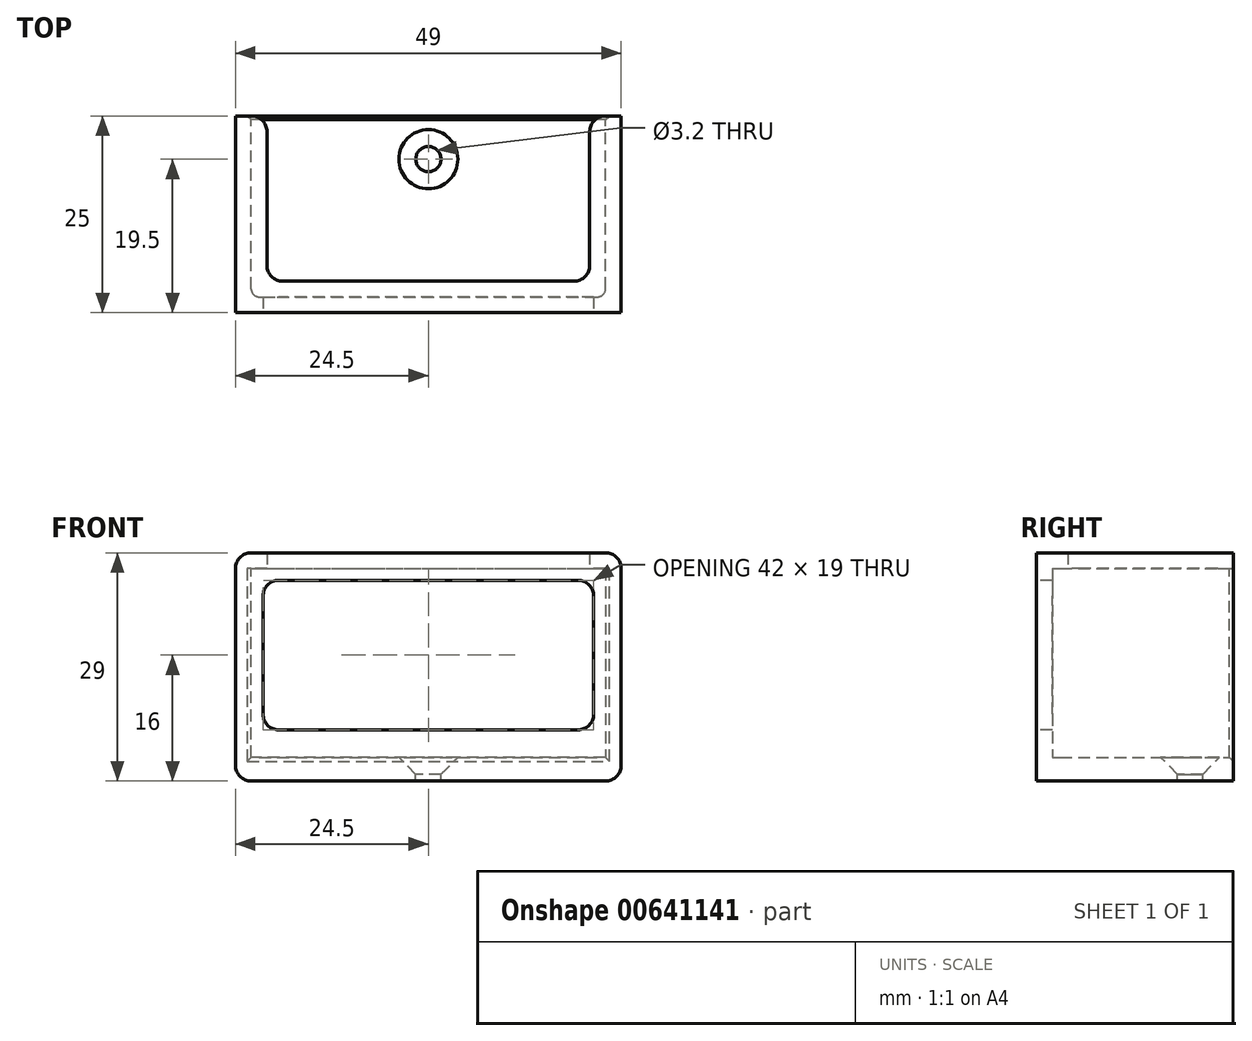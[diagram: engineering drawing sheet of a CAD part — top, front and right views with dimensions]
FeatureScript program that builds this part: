
annotation { "Feature Type Name" : "Feature", "Feature Type Description" : "" }
export const myFeature = defineFeature(function(context is Context, id is Id, definition is map)
    precondition{}
    {
        {
            var Q0;
            Q0=qCreatedBy(makeId("Top.planeOp"),FACE);
            var sketch = newSketch(context, id + "F0", { "sketchPlane" : qUnion([Q0])});
            skLineSegment(sketch, "E0.bottom", {"start": v(-22.5, -11.5) * mm, "end": v(22.5, -11.5) * mm});
            skLineSegment(sketch, "E0.left", {"start": v(-22.5, -11.5) * mm, "end": v(-22.5, 11.5) * mm});
            skLineSegment(sketch, "E0.right", {"start": v(22.5, -11.5) * mm, "end": v(22.5, 11.5) * mm});
            skPoint(sketch, "E0.middle", {"position": v(0, 0) * mm});
            skLineSegment(sketch, "E1.bottom", {"start": v(-24.5, -13.5) * mm, "end": v(24.5, -13.5) * mm});
            skLineSegment(sketch, "E1.left", {"start": v(-24.5, -13.5) * mm, "end": v(-24.5, 11.5) * mm});
            skLineSegment(sketch, "E1.right", {"start": v(24.5, -13.5) * mm, "end": v(24.5, 11.5) * mm});
            skLineSegment(sketch, "E2", {"start": v(-22.5, 11.5) * mm, "end": v(-24.5, 11.5) * mm});
            skLineSegment(sketch, "E3", {"start": v(22.5, 11.5) * mm, "end": v(24.5, 11.5) * mm});
            skPoint(sketch, "E4.orphan", {"position": v(-24.5, 13.5) * mm});
            skPoint(sketch, "E5.orphan", {"position": v(24.5, 13.5) * mm});
            skSolve(sketch);
        }
        {
            var Q0;
            Q0 = qSketchRegion(id + "F0", true);
            extrude(context, id + "F1", {"entities" : qUnion([Q0]), "depth" : 24 * mm, "offsetDistance" : 25 * mm});
        }
        {
            var Q0;
            Q0=makeQuery(id+"F1.opExtrude","CAP_FACE",FACE,{"disambiguationData":[OSD([sQuery(id+"F0.wireOp",EDGE,"E0.bottom"),sQuery(id+"F0.wireOp",EDGE,"E0.left"),sQuery(id+"F0.wireOp",EDGE,"E0.right"),sQuery(id+"F0.wireOp",EDGE,"E1.bottom"),sQuery(id+"F0.wireOp",EDGE,"E1.left"),sQuery(id+"F0.wireOp",EDGE,"E1.right"),sQuery(id+"F0.wireOp",EDGE,"E2"),sQuery(id+"F0.wireOp",EDGE,"E3")])],"isStart":false});
            var sketch = newSketch(context, id + "F2", { "sketchPlane" : qUnion([Q0])});
            skLineSegment(sketch, "E6.bottom", {"start": v(-24.5, -13.5) * mm, "end": v(24.5, -13.5) * mm});
            skLineSegment(sketch, "E6.top", {"start": v(-24.5, -9.5) * mm, "end": v(24.5, -9.5) * mm});
            skLineSegment(sketch, "E6.left", {"start": v(-24.5, -13.5) * mm, "end": v(-24.5, -9.5) * mm});
            skLineSegment(sketch, "E6.right", {"start": v(24.5, -13.5) * mm, "end": v(24.5, -9.5) * mm});
            skLineSegment(sketch, "E7.bottom", {"start": v(-24.5, 11.5) * mm, "end": v(-20.5, 11.5) * mm});
            skLineSegment(sketch, "E7.top", {"start": v(-24.5, -9.5) * mm, "end": v(-20.5, -9.5) * mm});
            skLineSegment(sketch, "E7.left", {"start": v(-24.5, 11.5) * mm, "end": v(-24.5, -9.5) * mm});
            skLineSegment(sketch, "E7.right", {"start": v(-20.5, 11.5) * mm, "end": v(-20.5, -9.5) * mm});
            skLineSegment(sketch, "E8.bottom", {"start": v(24.5, 11.5) * mm, "end": v(20.5, 11.5) * mm});
            skLineSegment(sketch, "E8.top", {"start": v(24.5, -9.5) * mm, "end": v(20.5, -9.5) * mm});
            skLineSegment(sketch, "E8.left", {"start": v(24.5, 11.5) * mm, "end": v(24.5, -9.5) * mm});
            skLineSegment(sketch, "E8.right", {"start": v(20.5, 11.5) * mm, "end": v(20.5, -9.5) * mm});
            skSolve(sketch);
        }
        {
            var Q0;
            Q0 = qSketchRegion(id + "F2", true);
            extrude(context, id + "F3", {"entities" : qUnion([Q0]), "operationType" : NewBodyOperationType.ADD, "depth" : 2 * mm, "offsetDistance" : 25 * mm});
        }
        {
            var Q0;
            Q0=makeQuery(id+"F3.boolean.opBoolean","MERGE",FACE,{"derivedFrom":[makeQuery(id+"F1.opExtrude","SWEPT_FACE",FACE,{"disambiguationData":[OSD([sQuery(id+"F0.wireOp",EDGE,"E1.bottom")])]}),makeQuery(id+"F3.opExtrude","SWEPT_FACE",FACE,{"disambiguationData":[OSD([sQuery(id+"F2.wireOp",EDGE,"E6.bottom")])]})]});
            var sketch = newSketch(context, id + "F4", { "sketchPlane" : qUnion([Q0])});
            skLineSegment(sketch, "E9.bottom", {"start": v(-21, 22.5) * mm, "end": v(21, 22.5) * mm});
            skLineSegment(sketch, "E9.top", {"start": v(-21, 3.5) * mm, "end": v(21, 3.5) * mm});
            skLineSegment(sketch, "E9.left", {"start": v(-21, 22.5) * mm, "end": v(-21, 3.5) * mm});
            skLineSegment(sketch, "E9.right", {"start": v(21, 22.5) * mm, "end": v(21, 3.5) * mm});
            skSolve(sketch);
        }
        {
            var Q0;
            Q0 = qSketchRegion(id + "F4", true);
            extrude(context, id + "F5", {"entities" : qUnion([Q0]), "operationType" : NewBodyOperationType.REMOVE, "oppositeDirection" : true, "depth" : 25 * mm, "offsetDistance" : 25 * mm});
        }
        {
            var Q0;
            Q0=makeQuery(id+"F1.opExtrude","CAP_FACE",FACE,{"disambiguationData":[OSD([sQuery(id+"F0.wireOp",EDGE,"E0.bottom"),sQuery(id+"F0.wireOp",EDGE,"E0.left"),sQuery(id+"F0.wireOp",EDGE,"E0.right"),sQuery(id+"F0.wireOp",EDGE,"E1.bottom"),sQuery(id+"F0.wireOp",EDGE,"E1.left"),sQuery(id+"F0.wireOp",EDGE,"E1.right"),sQuery(id+"F0.wireOp",EDGE,"E2"),sQuery(id+"F0.wireOp",EDGE,"E3")])],"isStart":true});
            var sketch = newSketch(context, id + "F6", { "sketchPlane" : qUnion([Q0])});
            skLineSegment(sketch, "E10.bottom", {"start": v(24.5, 13.5) * mm, "end": v(-24.5, 13.5) * mm});
            skLineSegment(sketch, "E10.top", {"start": v(24.5, -11.5) * mm, "end": v(-24.5, -11.5) * mm});
            skLineSegment(sketch, "E10.left", {"start": v(24.5, 13.5) * mm, "end": v(24.5, -11.5) * mm});
            skLineSegment(sketch, "E10.right", {"start": v(-24.5, 13.5) * mm, "end": v(-24.5, -11.5) * mm});
            skSolve(sketch);
        }
        {
            var Q0;
            Q0 = qSketchRegion(id + "F6", true);
            extrude(context, id + "F7", {"entities" : qUnion([Q0]), "operationType" : NewBodyOperationType.ADD, "depth" : 3 * mm, "offsetDistance" : 25 * mm});
        }
        {
            var Q0;
            Q0=makeQuery(id+"F5.boolean.opBoolean","COPY",EDGE,{"derivedFrom":makeQuery(id+"F5.opExtrude","SWEPT_EDGE",EDGE,{"disambiguationData":[OSD([sQuery(id+"F4.wireOp",EDGE,"E9.top"),sQuery(id+"F4.wireOp",EDGE,"E9.left")])]})});
            var Q1;
            Q1=makeQuery(id+"F5.boolean.opBoolean","COPY",EDGE,{"derivedFrom":makeQuery(id+"F5.opExtrude","SWEPT_EDGE",EDGE,{"disambiguationData":[OSD([sQuery(id+"F4.wireOp",EDGE,"E9.top"),sQuery(id+"F4.wireOp",EDGE,"E9.right")])]})});
            var Q2;
            Q2=makeQuery(id+"F5.boolean.opBoolean","COPY",EDGE,{"derivedFrom":makeQuery(id+"F5.opExtrude","SWEPT_EDGE",EDGE,{"disambiguationData":[OSD([sQuery(id+"F4.wireOp",EDGE,"E9.bottom"),sQuery(id+"F4.wireOp",EDGE,"E9.left")])]})});
            var Q3;
            Q3=makeQuery(id+"F5.boolean.opBoolean","COPY",EDGE,{"derivedFrom":makeQuery(id+"F5.opExtrude","SWEPT_EDGE",EDGE,{"disambiguationData":[OSD([sQuery(id+"F4.wireOp",EDGE,"E9.bottom"),sQuery(id+"F4.wireOp",EDGE,"E9.right")])]})});
            var Q4;
            Q4=makeQuery(id+"F7.opExtrude","CAP_EDGE",EDGE,{"disambiguationData":[OSD([sQuery(id+"F6.wireOp",EDGE,"E10.right")])],"isStart":false});
            var Q5;
            Q5=makeQuery(id+"F7.opExtrude","CAP_EDGE",EDGE,{"disambiguationData":[OSD([sQuery(id+"F6.wireOp",EDGE,"E10.left")])],"isStart":false});
            var Q6;
            Q6=makeQuery(id+"F3.opExtrude","SWEPT_EDGE",EDGE,{"disambiguationData":[OSD([sQuery(id+"F2.wireOp",EDGE,"E6.top"),sQuery(id+"F2.wireOp",EDGE,"E7.top"),sQuery(id+"F2.wireOp",EDGE,"E7.right")])]});
            var Q7;
            Q7=makeQuery(id+"F3.opExtrude","SWEPT_EDGE",EDGE,{"disambiguationData":[OSD([sQuery(id+"F2.wireOp",EDGE,"E6.top"),sQuery(id+"F2.wireOp",EDGE,"E8.top"),sQuery(id+"F2.wireOp",EDGE,"E8.right")])]});
            var Q8;
            Q8=makeQuery(id+"F3.opExtrude","SWEPT_EDGE",EDGE,{"disambiguationData":[OSD([sQuery(id+"F2.wireOp",EDGE,"E8.bottom"),sQuery(id+"F2.wireOp",EDGE,"E8.right")])]});
            var Q9;
            Q9=makeQuery(id+"F3.opExtrude","SWEPT_EDGE",EDGE,{"disambiguationData":[OSD([sQuery(id+"F2.wireOp",EDGE,"E7.bottom"),sQuery(id+"F2.wireOp",EDGE,"E7.right")])]});
            var Q10;
            Q10=makeQuery(id+"F3.opExtrude","CAP_EDGE",EDGE,{"disambiguationData":[OSD([sQuery(id+"F2.wireOp",EDGE,"E6.right"),sQuery(id+"F2.wireOp",EDGE,"E8.left")])],"isStart":false});
            var Q11;
            Q11=makeQuery(id+"F3.opExtrude","CAP_EDGE",EDGE,{"disambiguationData":[OSD([sQuery(id+"F2.wireOp",EDGE,"E6.left"),sQuery(id+"F2.wireOp",EDGE,"E7.left")])],"isStart":false});
            fillet(context, id + "F8", {"entities" : qUnion([Q0, Q1, Q2, Q3, Q4, Q5, Q6, Q7, Q8, Q9, Q10, Q11]), "radius" : 2 * mm, "tangentPropagation" : true, "allowEdgeOverflow" : false});
        }
        {
            var Q0;
            Q0=makeQuery(id+"F7.opExtrude","CAP_FACE",FACE,{"disambiguationData":[OSD([sQuery(id+"F6.wireOp",EDGE,"E10.bottom"),sQuery(id+"F6.wireOp",EDGE,"E10.top"),sQuery(id+"F6.wireOp",EDGE,"E10.left"),sQuery(id+"F6.wireOp",EDGE,"E10.right")])],"isStart":true});
            var sketch = newSketch(context, id + "F9", { "sketchPlane" : qUnion([Q0])});
            skLineSegment(sketch, "E11", {"start": v(0, 0) * mm, "end": v(0, 6) * mm});
            skSolve(sketch);
        }
        {
            var Q0;
            Q0=sQuery(id+"F9.wireOp",VERTEX,"E11.end");
            var Q1;
            Q1=makeQuery(id+"F1.opExtrude","SWEPT_BODY",BODY,{"disambiguationData":[OSD([sQuery(id+"F0.wireOp",EDGE,"E0.bottom"),sQuery(id+"F0.wireOp",EDGE,"E0.left"),sQuery(id+"F0.wireOp",EDGE,"E0.right"),sQuery(id+"F0.wireOp",EDGE,"E1.bottom"),sQuery(id+"F0.wireOp",EDGE,"E1.left"),sQuery(id+"F0.wireOp",EDGE,"E1.right"),sQuery(id+"F0.wireOp",EDGE,"E2"),sQuery(id+"F0.wireOp",EDGE,"E3")])]});
            hole(context, id + "F10", {"style" : HoleStyle.C_SINK, "endStyle" : HoleEndStyle.THROUGH, "holeDiameter" : 3.2 * mm, "cSinkDiameter" : 7.5 * mm, "cSinkAngle" : 90 * degree, "majorDiameter" : 5 * mm, "isTappedThrough" : true, "tappedDepth" : 12 * mm, "tapClearance" : 3, "locations" : qUnion([Q0]), "scope" : qUnion([Q1])});
        }
        {
            var Q0;
            Q0=makeQuery(id+"F1.opExtrude","SWEPT_EDGE",EDGE,{"disambiguationData":[OSD([sQuery(id+"F0.wireOp",EDGE,"E0.bottom"),sQuery(id+"F0.wireOp",EDGE,"E0.left")])]});
            var Q1;
            Q1=makeQuery(id+"F1.opExtrude","SWEPT_EDGE",EDGE,{"disambiguationData":[OSD([sQuery(id+"F0.wireOp",EDGE,"E0.bottom"),sQuery(id+"F0.wireOp",EDGE,"E0.right")])]});
            fillet(context, id + "F11", {"entities" : qUnion([Q0, Q1]), "radius" : 1 * mm, "tangentPropagation" : true, "allowEdgeOverflow" : false});
        }
        {
            var Q0;
            Q0=makeQuery(id+"F1.opExtrude","SWEPT_EDGE",EDGE,{"disambiguationData":[OSD([sQuery(id+"F0.wireOp",EDGE,"E0.left"),sQuery(id+"F0.wireOp",EDGE,"E2")])]});
            var Q1;
            Q1=makeQuery(id+"F7.opExtrude","CAP_EDGE",EDGE,{"disambiguationData":[OSD([sQuery(id+"F6.wireOp",EDGE,"E10.top")])],"isStart":true});
            var Q2;
            Q2=makeQuery(id+"F1.opExtrude","SWEPT_EDGE",EDGE,{"disambiguationData":[OSD([sQuery(id+"F0.wireOp",EDGE,"E0.right"),sQuery(id+"F0.wireOp",EDGE,"E3")])]});
            chamfer(context, id + "F12", {"entities" : qUnion([Q0, Q1, Q2]), "width" : 0.5 * mm, "tangentPropagation" : true});
        }
    });
